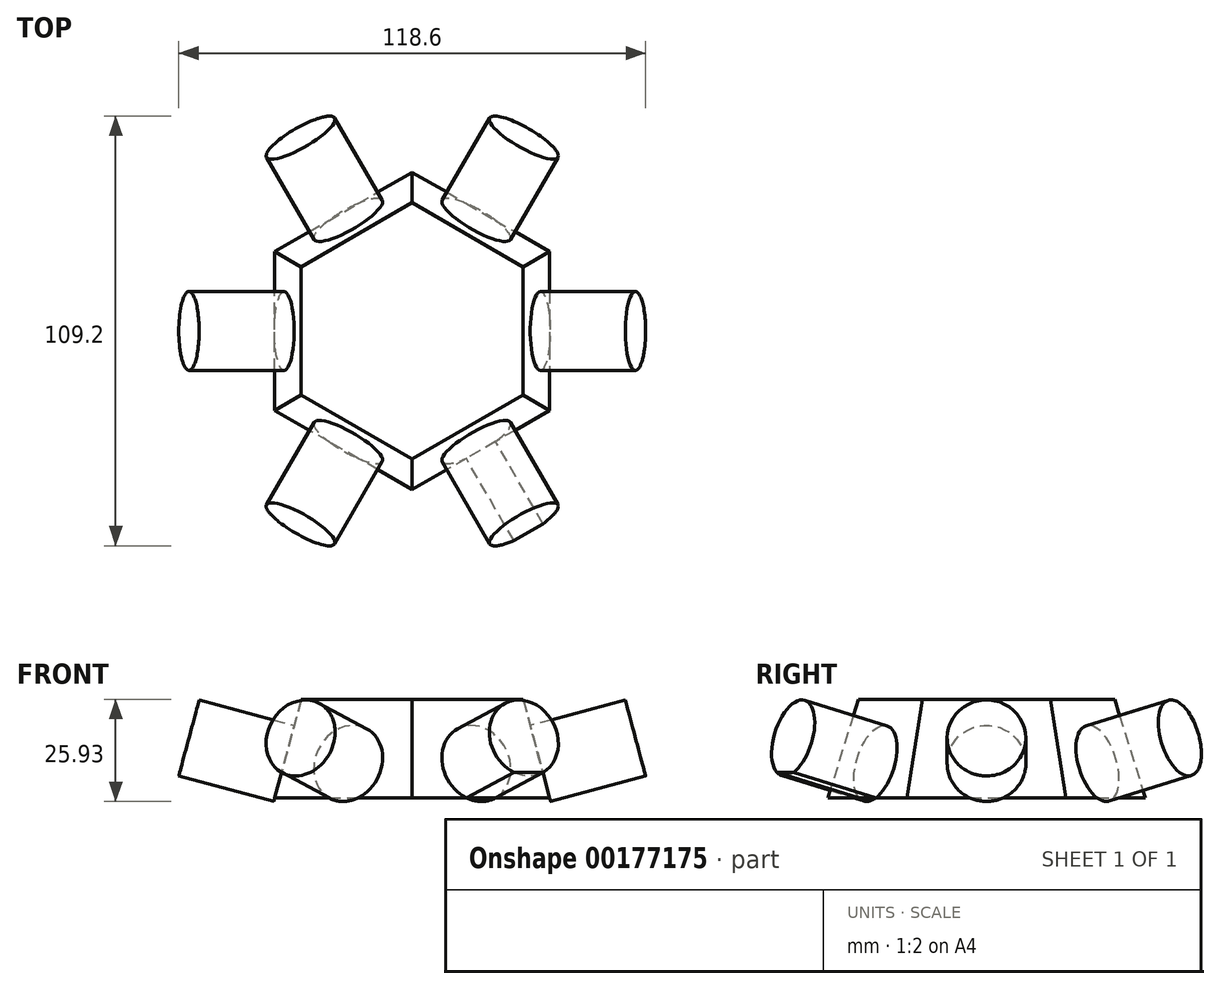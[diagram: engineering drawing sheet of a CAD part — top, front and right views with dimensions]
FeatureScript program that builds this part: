
annotation { "Feature Type Name" : "Feature", "Feature Type Description" : "" }
export const myFeature = defineFeature(function(context is Context, id is Id, definition is map)
    precondition{}
    {
        {
            var Q0;
            Q0=qCreatedBy(makeId("Top.planeOp"),FACE);
            var sketch = newSketch(context, id + "F0", { "sketchPlane" : qUnion([Q0])});
            skCircle(sketch, "E0.cCircle", {"center": v(0, 0) * mm, "radius": 34.9 * mm, "construction": true});
            skLineSegment(sketch, "E0.0", {"start": v(-34.9, -20.15) * mm, "end": v(-34.9, 20.15) * mm});
            skLineSegment(sketch, "E0.1", {"start": v(-34.9, 20.15) * mm, "end": v(0, 40.3) * mm});
            skLineSegment(sketch, "E0.2", {"start": v(0, 40.3) * mm, "end": v(34.9, 20.15) * mm});
            skLineSegment(sketch, "E0.3", {"start": v(34.9, 20.15) * mm, "end": v(34.9, -20.15) * mm});
            skLineSegment(sketch, "E0.4", {"start": v(34.9, -20.15) * mm, "end": v(0, -40.3) * mm});
            skLineSegment(sketch, "E0.5", {"start": v(0, -40.3) * mm, "end": v(-34.9, -20.15) * mm});
            skPoint(sketch, "E0.0.midPoint", {"position": v(-34.9, 0) * mm});
            skSolve(sketch);
        }
        {
            var Q0;
            Q0=makeQuery(id+"F0.imprint","IMPRINT",FACE,{"disambiguationData":[TD([[makeQuery(id+"F0.imprint","IMPRINT",EDGE,{"derivedFrom":sQuery(id+"F0.wireOp",EDGE,"E0.0")}),-1.0]])]});
            extrude(context, id + "F1", {"entities" : qUnion([Q0]), "depth" : 25 * mm, "hasDraft" : true, "draftAngle" : 15 * degree, "draftPullDirection" : true});
        }
        {
            var Q0;
            Q0=makeQuery(id+"F1.opExtrude","SWEPT_FACE",FACE,{"disambiguationData":[OSD([sQuery(id+"F0.wireOp",EDGE,"E0.5")])]});
            var sketch = newSketch(context, id + "F2", { "sketchPlane" : qUnion([Q0])});
            skCircle(sketch, "E1", {"center": v(0, 0) * mm, "radius": 10 * mm});
            skSolve(sketch);
        }
        {
            var Q0;
            Q0 = qSketchRegion(id + "F2", true);
            extrude(context, id + "F3", {"entities" : qUnion([Q0]), "operationType" : NewBodyOperationType.ADD, "depth" : 25 * mm});
        }
        {
            var Q0;
            Q0=makeQuery(id+"F1.opExtrude","SWEPT_FACE",FACE,{"disambiguationData":[OSD([sQuery(id+"F0.wireOp",EDGE,"E0.4")])]});
            var sketch = newSketch(context, id + "F4", { "sketchPlane" : qUnion([Q0])});
            skCircle(sketch, "E2", {"center": v(0, 0) * mm, "radius": 10 * mm});
            skSolve(sketch);
        }
        {
            var Q0;
            {var subQ0=sQuery(id+"F4.wireOp",EDGE,"E2");var subQ1=makeQuery(id+"F1.opExtrude","CAP_EDGE",EDGE,{"disambiguationData":[OSD([sQuery(id+"F0.wireOp",EDGE,"E0.4")])],"isStart":true});var subQ2=makeQuery(id+"F4.imprint","INTERSECT",VERTEX,{"disambiguationData":[OD(0.0)],"derivedFrom":[subQ1,subQ0]});Q0=makeQuery(id+"F4.imprint","IMPRINT",FACE,{"disambiguationData":[TD([[makeQuery(id+"F4.imprint","IMPRINT",EDGE,{"disambiguationData":[TD([[subQ2,-1.0]])],"derivedFrom":subQ0}),1.0]])]});}
            extrude(context, id + "F8", {"entities" : qUnion([Q0]), "operationType" : NewBodyOperationType.ADD, "depth" : 25 * mm});
        }
        {
            var Q0;
            Q0=makeQuery(id+"F1.opExtrude","SWEPT_FACE",FACE,{"disambiguationData":[OSD([sQuery(id+"F0.wireOp",EDGE,"E0.3")])]});
            var sketch = newSketch(context, id + "F9", { "sketchPlane" : qUnion([Q0])});
            skCircle(sketch, "E3", {"center": v(0, 0) * mm, "radius": 10 * mm});
            skSolve(sketch);
        }
        {
            var Q0;
            Q0 = qSketchRegion(id + "F9", true);
            extrude(context, id + "F10", {"entities" : qUnion([Q0]), "operationType" : NewBodyOperationType.ADD, "depth" : 25 * mm});
        }
        {
            var Q0;
            Q0=makeQuery(id+"F1.opExtrude","SWEPT_FACE",FACE,{"disambiguationData":[OSD([sQuery(id+"F0.wireOp",EDGE,"E0.2")])]});
            var sketch = newSketch(context, id + "F11", { "sketchPlane" : qUnion([Q0])});
            skCircle(sketch, "E4", {"center": v(0, 0) * mm, "radius": 10 * mm});
            skSolve(sketch);
        }
        {
            var Q0;
            Q0 = qSketchRegion(id + "F11", true);
            extrude(context, id + "F12", {"entities" : qUnion([Q0]), "operationType" : NewBodyOperationType.ADD, "depth" : 25 * mm});
        }
        {
            var Q0;
            Q0=makeQuery(id+"F1.opExtrude","SWEPT_FACE",FACE,{"disambiguationData":[OSD([sQuery(id+"F0.wireOp",EDGE,"E0.1")])]});
            var sketch = newSketch(context, id + "F13", { "sketchPlane" : qUnion([Q0])});
            skCircle(sketch, "E5", {"center": v(0, 0) * mm, "radius": 10 * mm});
            skSolve(sketch);
        }
        {
            var Q0;
            Q0 = qSketchRegion(id + "F13", true);
            extrude(context, id + "F5", {"entities" : qUnion([Q0]), "operationType" : NewBodyOperationType.ADD, "depth" : 25 * mm});
        }
        {
            var Q0;
            Q0=makeQuery(id+"F1.opExtrude","SWEPT_FACE",FACE,{"disambiguationData":[OSD([sQuery(id+"F0.wireOp",EDGE,"E0.0")])]});
            var sketch = newSketch(context, id + "F6", { "sketchPlane" : qUnion([Q0])});
            skCircle(sketch, "E6", {"center": v(0, 0) * mm, "radius": 10 * mm});
            skSolve(sketch);
        }
        {
            var Q0;
            Q0 = qSketchRegion(id + "F6", true);
            extrude(context, id + "F7", {"entities" : qUnion([Q0]), "operationType" : NewBodyOperationType.ADD, "depth" : 25 * mm});
        }
    });
